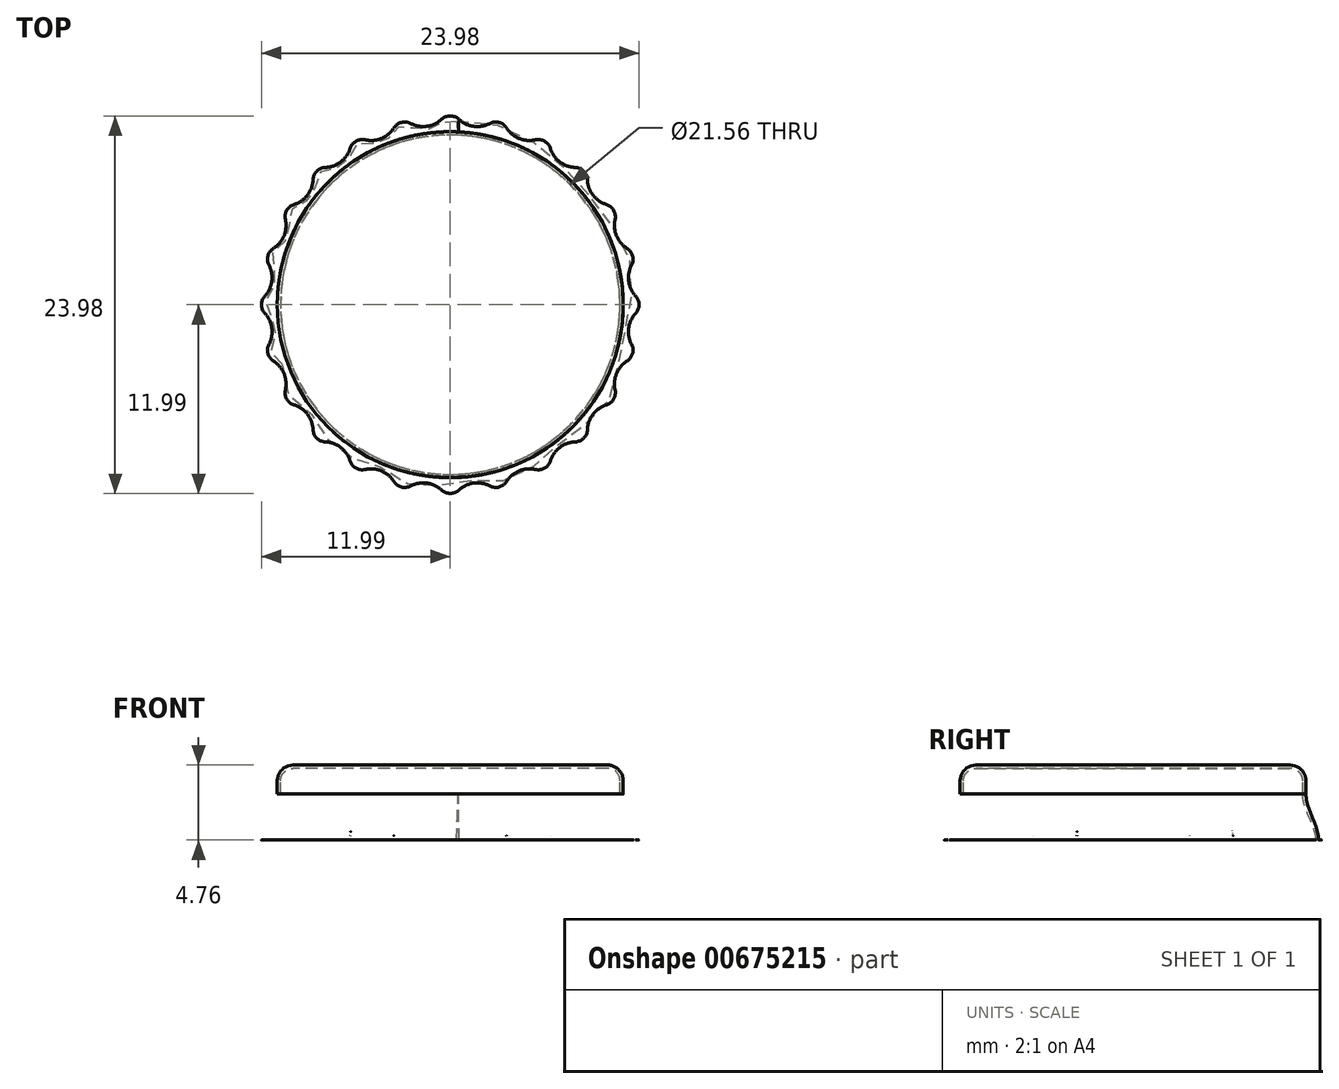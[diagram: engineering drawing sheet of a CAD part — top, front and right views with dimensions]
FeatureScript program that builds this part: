
annotation { "Feature Type Name" : "Feature", "Feature Type Description" : "" }
export const myFeature = defineFeature(function(context is Context, id is Id, definition is map)
    precondition{}
    {
        {
            var Q0;
            Q0=qCreatedBy(makeId("Top.planeOp"),FACE);
            var sketch = newSketch(context, id + "F0", { "sketchPlane" : qUnion([Q0])});
            skCircle(sketch, "E0", {"center": v(0, 0) * mm, "radius": 11.43 * mm, "construction": true});
            skCircle(sketch, "E1", {"center": v(0, 0) * mm, "radius": 10.99 * mm, "construction": true});
            skArc(sketch, "E2", {"start": v(0.55, 11.77) * mm, "mid": v(0.99, 11.48) * mm, "end": v(1.5, 11.33) * mm});
            skCircle(sketch, "E3", {"center": v(0, 0) * mm, "radius": 13.15 * mm, "construction": true});
            skLineSegment(sketch, "E4", {"start": v(0, 0) * mm, "end": v(0, 15.62) * mm, "construction": true});
            skArc(sketch, "E5", {"start": v(-1.5, 11.33) * mm, "mid": v(-0.99, 11.48) * mm, "end": v(-0.55, 11.77) * mm});
            skLineSegment(sketch, "E6", {"start": v(1.5, 11.33) * mm, "end": v(0, 0) * mm, "construction": true});
            skLineSegment(sketch, "E7", {"start": v(-1.5, 11.33) * mm, "end": v(0, 0) * mm, "construction": true});
            skPoint(sketch, "E8.visualSharp", {"position": v(0, 13.03) * mm});
            skArc(sketch, "E9.filletArc", {"start": v(0.55, 11.77) * mm, "mid": v(0, 11.99) * mm, "end": v(-0.55, 11.77) * mm});
            skArc(sketch, "E10.1.0", {"start": v(-2.51, 11.51) * mm, "mid": v(-3.1, 11.58) * mm, "end": v(-3.58, 11.23) * mm});
            skArc(sketch, "E10.1.1", {"start": v(-2.51, 11.51) * mm, "mid": v(-2.02, 11.34) * mm, "end": v(-1.5, 11.33) * mm});
            skArc(sketch, "E10.1.2", {"start": v(-4.37, 10.56) * mm, "mid": v(-3.93, 10.83) * mm, "end": v(-3.58, 11.23) * mm});
            skArc(sketch, "E10.2.0", {"start": v(-5.4, 10.47) * mm, "mid": v(-6, 10.38) * mm, "end": v(-6.36, 9.92) * mm});
            skArc(sketch, "E10.2.1", {"start": v(-5.4, 10.47) * mm, "mid": v(-4.88, 10.44) * mm, "end": v(-4.37, 10.56) * mm});
            skArc(sketch, "E10.2.2", {"start": v(-6.96, 9.07) * mm, "mid": v(-6.6, 9.45) * mm, "end": v(-6.36, 9.92) * mm});
            skArc(sketch, "E10.3.0", {"start": v(-7.93, 8.71) * mm, "mid": v(-8.48, 8.48) * mm, "end": v(-8.71, 7.93) * mm});
            skArc(sketch, "E10.3.1", {"start": v(-7.93, 8.71) * mm, "mid": v(-7.42, 8.82) * mm, "end": v(-6.96, 9.07) * mm});
            skArc(sketch, "E10.3.2", {"start": v(-9.07, 6.96) * mm, "mid": v(-8.82, 7.42) * mm, "end": v(-8.71, 7.93) * mm});
            skArc(sketch, "E10.4.0", {"start": v(-9.92, 6.36) * mm, "mid": v(-10.38, 6) * mm, "end": v(-10.47, 5.4) * mm});
            skArc(sketch, "E10.4.1", {"start": v(-9.92, 6.36) * mm, "mid": v(-9.45, 6.6) * mm, "end": v(-9.07, 6.96) * mm});
            skArc(sketch, "E10.4.2", {"start": v(-10.56, 4.37) * mm, "mid": v(-10.44, 4.88) * mm, "end": v(-10.47, 5.4) * mm});
            skArc(sketch, "E10.5.0", {"start": v(-11.23, 3.58) * mm, "mid": v(-11.58, 3.1) * mm, "end": v(-11.51, 2.51) * mm});
            skArc(sketch, "E10.5.1", {"start": v(-11.23, 3.58) * mm, "mid": v(-10.83, 3.93) * mm, "end": v(-10.56, 4.37) * mm});
            skArc(sketch, "E10.5.2", {"start": v(-11.33, 1.5) * mm, "mid": v(-11.34, 2.02) * mm, "end": v(-11.51, 2.51) * mm});
            skArc(sketch, "E10.6.0", {"start": v(-11.77, 0.55) * mm, "mid": v(-11.99, 0) * mm, "end": v(-11.77, -0.55) * mm});
            skArc(sketch, "E10.6.1", {"start": v(-11.77, 0.55) * mm, "mid": v(-11.48, 0.99) * mm, "end": v(-11.33, 1.5) * mm});
            skArc(sketch, "E10.6.2", {"start": v(-11.33, -1.5) * mm, "mid": v(-11.48, -0.99) * mm, "end": v(-11.77, -0.55) * mm});
            skArc(sketch, "E10.7.0", {"start": v(-11.51, -2.51) * mm, "mid": v(-11.58, -3.1) * mm, "end": v(-11.23, -3.58) * mm});
            skArc(sketch, "E10.7.1", {"start": v(-11.51, -2.51) * mm, "mid": v(-11.34, -2.02) * mm, "end": v(-11.33, -1.5) * mm});
            skArc(sketch, "E10.7.2", {"start": v(-10.56, -4.37) * mm, "mid": v(-10.83, -3.93) * mm, "end": v(-11.23, -3.58) * mm});
            skArc(sketch, "E10.8.0", {"start": v(-10.47, -5.4) * mm, "mid": v(-10.38, -6) * mm, "end": v(-9.92, -6.36) * mm});
            skArc(sketch, "E10.8.1", {"start": v(-10.47, -5.4) * mm, "mid": v(-10.44, -4.88) * mm, "end": v(-10.56, -4.37) * mm});
            skArc(sketch, "E10.8.2", {"start": v(-9.07, -6.96) * mm, "mid": v(-9.45, -6.6) * mm, "end": v(-9.92, -6.36) * mm});
            skArc(sketch, "E10.9.0", {"start": v(-8.71, -7.93) * mm, "mid": v(-8.48, -8.48) * mm, "end": v(-7.93, -8.71) * mm});
            skArc(sketch, "E10.9.1", {"start": v(-8.71, -7.93) * mm, "mid": v(-8.82, -7.42) * mm, "end": v(-9.07, -6.96) * mm});
            skArc(sketch, "E10.9.2", {"start": v(-6.96, -9.07) * mm, "mid": v(-7.42, -8.82) * mm, "end": v(-7.93, -8.71) * mm});
            skArc(sketch, "E10.10.0", {"start": v(-6.36, -9.92) * mm, "mid": v(-6, -10.38) * mm, "end": v(-5.4, -10.47) * mm});
            skArc(sketch, "E10.10.1", {"start": v(-6.36, -9.92) * mm, "mid": v(-6.6, -9.45) * mm, "end": v(-6.96, -9.07) * mm});
            skArc(sketch, "E10.10.2", {"start": v(-4.37, -10.56) * mm, "mid": v(-4.88, -10.44) * mm, "end": v(-5.4, -10.47) * mm});
            skArc(sketch, "E10.11.0", {"start": v(-3.58, -11.23) * mm, "mid": v(-3.1, -11.58) * mm, "end": v(-2.51, -11.51) * mm});
            skArc(sketch, "E10.11.1", {"start": v(-3.58, -11.23) * mm, "mid": v(-3.93, -10.83) * mm, "end": v(-4.37, -10.56) * mm});
            skArc(sketch, "E10.11.2", {"start": v(-1.5, -11.33) * mm, "mid": v(-2.02, -11.34) * mm, "end": v(-2.51, -11.51) * mm});
            skArc(sketch, "E10.12.0", {"start": v(-0.55, -11.77) * mm, "mid": v(0, -11.99) * mm, "end": v(0.55, -11.77) * mm});
            skArc(sketch, "E10.12.1", {"start": v(-0.55, -11.77) * mm, "mid": v(-0.99, -11.48) * mm, "end": v(-1.5, -11.33) * mm});
            skArc(sketch, "E10.12.2", {"start": v(1.5, -11.33) * mm, "mid": v(0.99, -11.48) * mm, "end": v(0.55, -11.77) * mm});
            skArc(sketch, "E10.13.0", {"start": v(2.51, -11.51) * mm, "mid": v(3.1, -11.58) * mm, "end": v(3.58, -11.23) * mm});
            skArc(sketch, "E10.13.1", {"start": v(2.51, -11.51) * mm, "mid": v(2.02, -11.34) * mm, "end": v(1.5, -11.33) * mm});
            skArc(sketch, "E10.13.2", {"start": v(4.37, -10.56) * mm, "mid": v(3.93, -10.83) * mm, "end": v(3.58, -11.23) * mm});
            skArc(sketch, "E10.14.0", {"start": v(5.4, -10.47) * mm, "mid": v(6, -10.38) * mm, "end": v(6.36, -9.92) * mm});
            skArc(sketch, "E10.14.1", {"start": v(5.4, -10.47) * mm, "mid": v(4.88, -10.44) * mm, "end": v(4.37, -10.56) * mm});
            skArc(sketch, "E10.14.2", {"start": v(6.96, -9.07) * mm, "mid": v(6.6, -9.45) * mm, "end": v(6.36, -9.92) * mm});
            skArc(sketch, "E10.15.0", {"start": v(7.93, -8.71) * mm, "mid": v(8.48, -8.48) * mm, "end": v(8.71, -7.93) * mm});
            skArc(sketch, "E10.15.1", {"start": v(7.93, -8.71) * mm, "mid": v(7.42, -8.82) * mm, "end": v(6.96, -9.07) * mm});
            skArc(sketch, "E10.15.2", {"start": v(9.07, -6.96) * mm, "mid": v(8.82, -7.42) * mm, "end": v(8.71, -7.93) * mm});
            skArc(sketch, "E10.16.0", {"start": v(9.92, -6.36) * mm, "mid": v(10.38, -6) * mm, "end": v(10.47, -5.4) * mm});
            skArc(sketch, "E10.16.1", {"start": v(9.92, -6.36) * mm, "mid": v(9.45, -6.6) * mm, "end": v(9.07, -6.96) * mm});
            skArc(sketch, "E10.16.2", {"start": v(10.56, -4.37) * mm, "mid": v(10.44, -4.88) * mm, "end": v(10.47, -5.4) * mm});
            skArc(sketch, "E10.17.0", {"start": v(11.23, -3.58) * mm, "mid": v(11.58, -3.1) * mm, "end": v(11.51, -2.51) * mm});
            skArc(sketch, "E10.17.1", {"start": v(11.23, -3.58) * mm, "mid": v(10.83, -3.93) * mm, "end": v(10.56, -4.37) * mm});
            skArc(sketch, "E10.17.2", {"start": v(11.33, -1.5) * mm, "mid": v(11.34, -2.02) * mm, "end": v(11.51, -2.51) * mm});
            skArc(sketch, "E10.18.0", {"start": v(11.77, -0.55) * mm, "mid": v(11.99, 0) * mm, "end": v(11.77, 0.55) * mm});
            skArc(sketch, "E10.18.1", {"start": v(11.77, -0.55) * mm, "mid": v(11.48, -0.99) * mm, "end": v(11.33, -1.5) * mm});
            skArc(sketch, "E10.18.2", {"start": v(11.33, 1.5) * mm, "mid": v(11.48, 0.99) * mm, "end": v(11.77, 0.55) * mm});
            skArc(sketch, "E10.19.0", {"start": v(11.51, 2.51) * mm, "mid": v(11.58, 3.1) * mm, "end": v(11.23, 3.58) * mm});
            skArc(sketch, "E10.19.1", {"start": v(11.51, 2.51) * mm, "mid": v(11.34, 2.02) * mm, "end": v(11.33, 1.5) * mm});
            skArc(sketch, "E10.19.2", {"start": v(10.56, 4.37) * mm, "mid": v(10.83, 3.93) * mm, "end": v(11.23, 3.58) * mm});
            skArc(sketch, "E10.20.0", {"start": v(10.47, 5.4) * mm, "mid": v(10.38, 6) * mm, "end": v(9.92, 6.36) * mm});
            skArc(sketch, "E10.20.1", {"start": v(10.47, 5.4) * mm, "mid": v(10.44, 4.88) * mm, "end": v(10.56, 4.37) * mm});
            skArc(sketch, "E10.20.2", {"start": v(9.07, 6.96) * mm, "mid": v(9.45, 6.6) * mm, "end": v(9.92, 6.36) * mm});
            skArc(sketch, "E10.21.0", {"start": v(8.71, 7.93) * mm, "mid": v(8.48, 8.48) * mm, "end": v(7.93, 8.71) * mm});
            skArc(sketch, "E10.21.1", {"start": v(8.71, 7.93) * mm, "mid": v(8.82, 7.42) * mm, "end": v(9.07, 6.96) * mm});
            skArc(sketch, "E10.21.2", {"start": v(6.96, 9.07) * mm, "mid": v(7.42, 8.82) * mm, "end": v(7.93, 8.71) * mm});
            skArc(sketch, "E10.22.0", {"start": v(6.36, 9.92) * mm, "mid": v(6, 10.38) * mm, "end": v(5.4, 10.47) * mm});
            skArc(sketch, "E10.22.1", {"start": v(6.36, 9.92) * mm, "mid": v(6.6, 9.45) * mm, "end": v(6.96, 9.07) * mm});
            skArc(sketch, "E10.22.2", {"start": v(4.37, 10.56) * mm, "mid": v(4.88, 10.44) * mm, "end": v(5.4, 10.47) * mm});
            skArc(sketch, "E10.23.0", {"start": v(3.58, 11.23) * mm, "mid": v(3.1, 11.58) * mm, "end": v(2.51, 11.51) * mm});
            skArc(sketch, "E10.23.1", {"start": v(3.58, 11.23) * mm, "mid": v(3.93, 10.83) * mm, "end": v(4.37, 10.56) * mm});
            skArc(sketch, "E10.23.2", {"start": v(1.5, 11.33) * mm, "mid": v(2.02, 11.34) * mm, "end": v(2.51, 11.51) * mm});
            skSolve(sketch);
        }
        {
            var Q0;
            Q0=makeQuery(id+"F0.imprint","IMPRINT",FACE,{"disambiguationData":[TD([[makeQuery(id+"F0.imprint","IMPRINT",EDGE,{"derivedFrom":sQuery(id+"F0.wireOp",EDGE,"E2")}),-1.0]])]});
            cPlane(context, id + "F1", {"entities" : qUnion([Q0]), "cplaneType" : CPlaneType.OFFSET, "offset" : 4.76 * mm, "width" : 152.4 * mm, "height" : 152.4 * mm});
        }
        {
            var Q0;
            Q0=qCreatedBy(id+"F1.planeOp",FACE);
            var sketch = newSketch(context, id + "F2", { "sketchPlane" : qUnion([Q0])});
            skCircle(sketch, "E11.0", {"center": v(0, 0) * mm, "radius": 10.99 * mm});
            skSolve(sketch);
        }
        {
            var Q0;
            Q0=makeQuery(id+"F0.imprint","IMPRINT",FACE,{"disambiguationData":[TD([[makeQuery(id+"F0.imprint","IMPRINT",EDGE,{"derivedFrom":sQuery(id+"F0.wireOp",EDGE,"E2")}),-1.0]])]});
            cPlane(context, id + "F3", {"entities" : qUnion([Q0]), "cplaneType" : CPlaneType.OFFSET, "offset" : 2.92 * mm, "width" : 152.4 * mm, "height" : 152.4 * mm});
        }
        {
            var Q0;
            Q0=qCreatedBy(id+"F3.planeOp",FACE);
            var sketch = newSketch(context, id + "F4", { "sketchPlane" : qUnion([Q0])});
            skCircle(sketch, "E12", {"center": v(0, 0) * mm, "radius": 10.99 * mm});
            skSolve(sketch);
        }
        {
            var Q0;
            Q0=makeQuery(id+"F0.imprint","IMPRINT",FACE,{"disambiguationData":[TD([[makeQuery(id+"F0.imprint","IMPRINT",EDGE,{"derivedFrom":sQuery(id+"F0.wireOp",EDGE,"E2")}),-1.0]])]});
            var Q1;
            Q1=makeQuery(id+"F4.imprint","IMPRINT",FACE,{"disambiguationData":[TD([[makeQuery(id+"F4.imprint","IMPRINT",EDGE,{"derivedFrom":sQuery(id+"F4.wireOp",EDGE,"E12")}),1.0]])]});
            loft(context, id + "F5", {"startCondition" : LoftEndDerivativeType.NORMAL_TO_PROFILE, "startMagnitude" : 1, "endCondition" : LoftEndDerivativeType.NORMAL_TO_PROFILE, "endMagnitude" : 1, "sheetProfilesArray" : [{ "sheetProfileEntities" : qUnion([Q0]) }, { "sheetProfileEntities" : qUnion([Q1]) }]});
        }
        {
            var Q1;
            Q1=makeQuery(id+"F5.opLoft","CAP_FACE",FACE,{"disambiguationData":[OSD([makeQuery(id+"F4.imprint","IMPRINT",FACE,{"disambiguationData":[TD([[makeQuery(id+"F4.imprint","IMPRINT",EDGE,{"derivedFrom":sQuery(id+"F4.wireOp",EDGE,"E12")}),1.0]])]})])],"isStart":true});
            var Q2;
            Q2=makeQuery(id+"F2.imprint","IMPRINT",FACE,{"disambiguationData":[TD([[makeQuery(id+"F2.imprint","IMPRINT",EDGE,{"derivedFrom":sQuery(id+"F2.wireOp",EDGE,"E11.0")}),1.0]])]});
            loft(context, id + "F6", {"operationType" : NewBodyOperationType.ADD, "startCondition" : LoftEndDerivativeType.NORMAL_TO_PROFILE, "startMagnitude" : 1, "endCondition" : LoftEndDerivativeType.NORMAL_TO_PROFILE, "endMagnitude" : 1, "sheetProfilesArray" : [{ "sheetProfileEntities" : qUnion([Q1]) }, { "sheetProfileEntities" : qUnion([Q2]) }]});
        }
        {
            var Q0;
            Q0=makeQuery(id+"F6.opLoft","MID_CAP_EDGE",EDGE,{"disambiguationData":[OSD([sQuery(id+"F0.wireOp",EDGE,"E2"),sQuery(id+"F0.wireOp",EDGE,"E9.filletArc"),sQuery(id+"F2.wireOp",EDGE,"E11.0"),sQuery(id+"F4.wireOp",EDGE,"E12")])],"capPos":1.0});
            fillet(context, id + "F7", {"entities" : qUnion([Q0]), "radius" : 1.02 * mm, "tangentPropagation" : true, "allowEdgeOverflow" : false});
        }
        {
            var Q0;
            Q0=makeQuery(id+"F5.opLoft","CAP_FACE",FACE,{"disambiguationData":[OSD([makeQuery(id+"F0.imprint","IMPRINT",FACE,{"disambiguationData":[TD([[makeQuery(id+"F0.imprint","IMPRINT",EDGE,{"derivedFrom":sQuery(id+"F0.wireOp",EDGE,"E2")}),-1.0]])]})])],"isStart":true});
            shell(context, id + "F8", {"entities" : qUnion([Q0]), "thickness" : 0.2 * mm});
        }
    });
